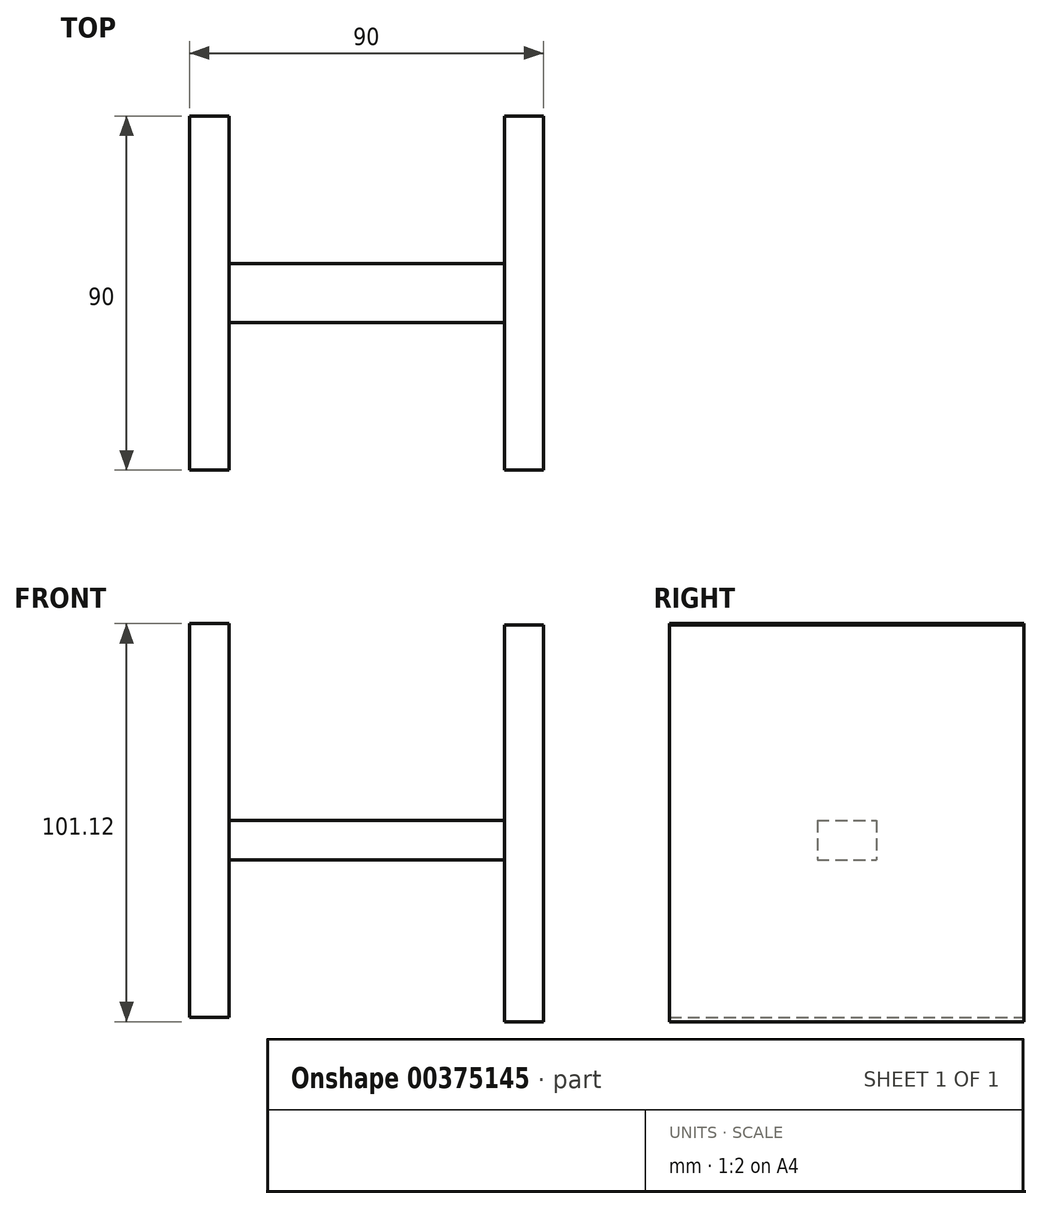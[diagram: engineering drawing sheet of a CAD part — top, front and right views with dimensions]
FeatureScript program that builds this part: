
annotation { "Feature Type Name" : "Feature", "Feature Type Description" : "" }
export const myFeature = defineFeature(function(context is Context, id is Id, definition is map)
    precondition{}
    {
        {
            var Q0;
            Q0=qCreatedBy(makeId("Front.planeOp"),FACE);
            var sketch = newSketch(context, id + "F0", { "sketchPlane" : qUnion([Q0])});
            skLineSegment(sketch, "E0.bottom", {"start": v(-45, 34.06) * mm, "end": v(-35, 34.06) * mm});
            skLineSegment(sketch, "E0.top", {"start": v(-45, -65.94) * mm, "end": v(-35, -65.94) * mm});
            skLineSegment(sketch, "E0.left", {"start": v(-45, 34.06) * mm, "end": v(-45, -65.94) * mm});
            skLineSegment(sketch, "E0.right", {"start": v(-35, 34.06) * mm, "end": v(-35, -65.94) * mm});
            skLineSegment(sketch, "E1.bottom", {"start": v(35, 33.78) * mm, "end": v(45, 33.78) * mm});
            skLineSegment(sketch, "E1.top", {"start": v(35, -67.06) * mm, "end": v(45, -67.06) * mm});
            skLineSegment(sketch, "E1.left", {"start": v(35, 33.78) * mm, "end": v(35, -67.06) * mm});
            skLineSegment(sketch, "E1.right", {"start": v(45, 33.78) * mm, "end": v(45, -67.06) * mm});
            skLineSegment(sketch, "E2.bottom", {"start": v(-35, -15.94) * mm, "end": v(35, -15.94) * mm});
            skLineSegment(sketch, "E2.top", {"start": v(-35, -25.94) * mm, "end": v(35, -25.94) * mm});
            skLineSegment(sketch, "E2.left", {"start": v(-35, -15.94) * mm, "end": v(-35, -25.94) * mm});
            skLineSegment(sketch, "E2.right", {"start": v(35, -15.94) * mm, "end": v(35, -25.94) * mm});
            skSolve(sketch);
        }
        {
            var Q0;
            {var subQ1=sQuery(id+"F0.wireOp",EDGE,"E0.bottom");Q0=makeQuery(id+"F0.imprint","IMPRINT",FACE,{"disambiguationData":[TD([[makeQuery(id+"F0.imprint","IMPRINT",EDGE,{"derivedFrom":subQ1}),-1.0]])]});}
            var Q1;
            {var subQ3=sQuery(id+"F0.wireOp",EDGE,"E1.bottom");Q1=makeQuery(id+"F0.imprint","IMPRINT",FACE,{"disambiguationData":[TD([[makeQuery(id+"F0.imprint","IMPRINT",EDGE,{"derivedFrom":subQ3}),-1.0]])]});}
            extrude(context, id + "F1", {"entities" : qUnion([Q0, Q1]), "endBound" : BoundingType.SYMMETRIC, "depth" : 90 * mm});
        }
        {
            var Q0;
            Q0=makeQuery(id+"F0.imprint","IMPRINT",FACE,{"disambiguationData":[TD([[makeQuery(id+"F0.imprint","IMPRINT",EDGE,{"derivedFrom":sQuery(id+"F0.wireOp",EDGE,"E2.bottom")}),-1.0]])]});
            extrude(context, id + "F2", {"entities" : qUnion([Q0]), "endBound" : BoundingType.SYMMETRIC, "depth" : 15 * mm});
        }
    });
